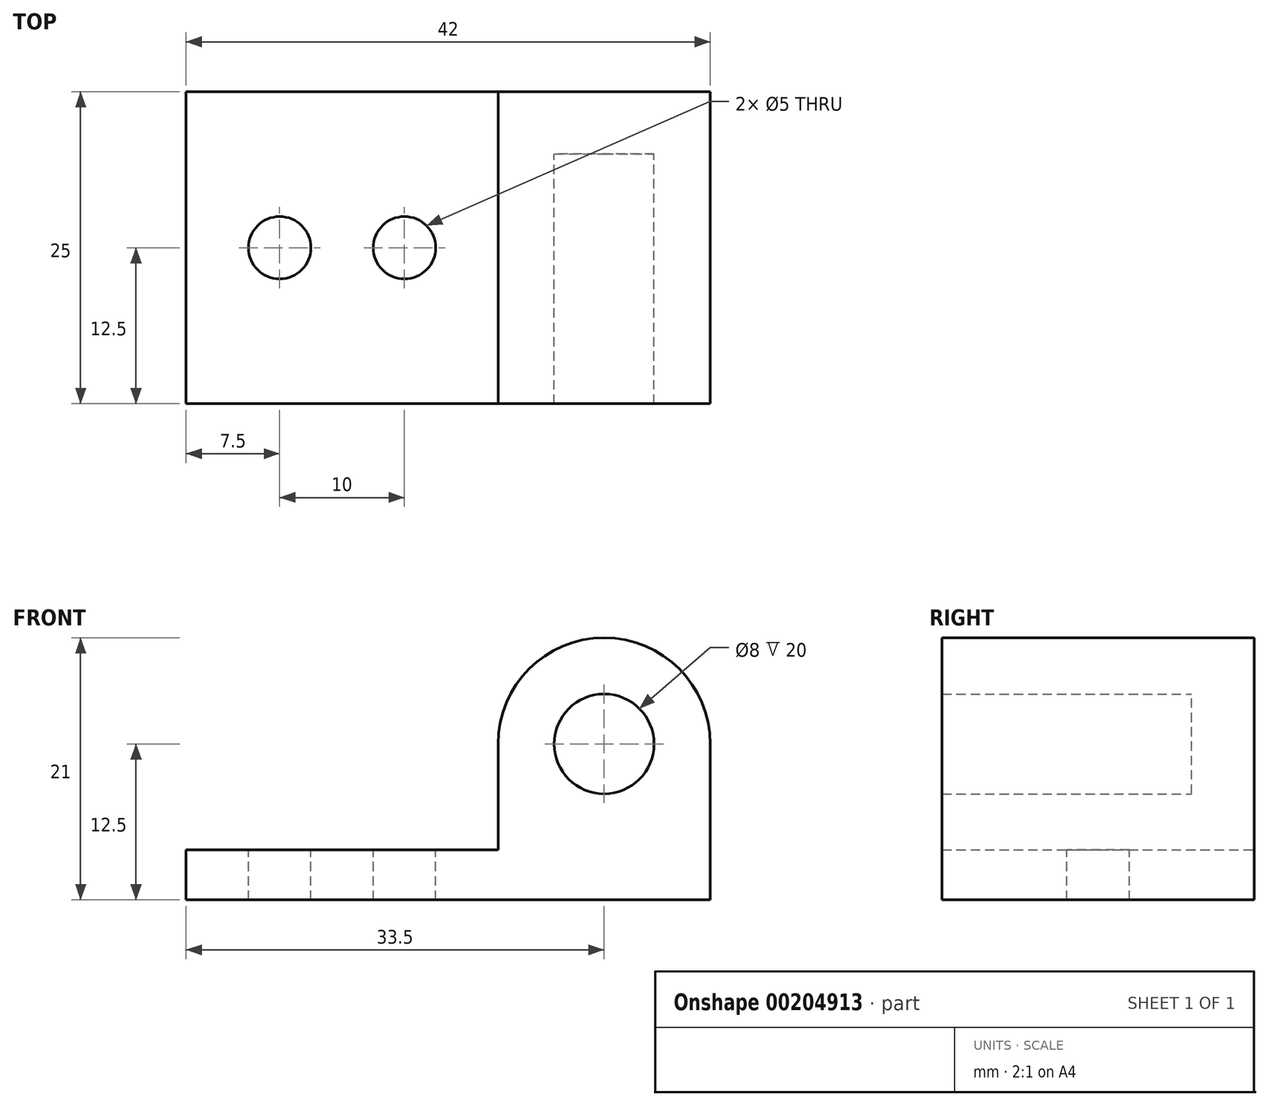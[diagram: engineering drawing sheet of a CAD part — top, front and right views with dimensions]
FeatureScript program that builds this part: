
annotation { "Feature Type Name" : "Feature", "Feature Type Description" : "" }
export const myFeature = defineFeature(function(context is Context, id is Id, definition is map)
    precondition{}
    {
        {
            var Q0;
            Q0=qCreatedBy(makeId("Front.planeOp"),FACE);
            var sketch = newSketch(context, id + "F0", { "sketchPlane" : qUnion([Q0])});
            skLineSegment(sketch, "E0", {"start": v(0, 0) * mm, "end": v(42, 0) * mm});
            skLineSegment(sketch, "E1", {"start": v(42, 0) * mm, "end": v(42, 4) * mm});
            skLineSegment(sketch, "E2", {"start": v(42, 4) * mm, "end": v(0, 4) * mm});
            skLineSegment(sketch, "E3", {"start": v(0, 4) * mm, "end": v(0, 0) * mm});
            skCircle(sketch, "E4", {"center": v(33.5, 12.5) * mm, "radius": 4 * mm});
            skCircle(sketch, "E5", {"center": v(33.5, 12.5) * mm, "radius": 8.5 * mm});
            skLineSegment(sketch, "E6", {"start": v(42, 4) * mm, "end": v(42, 21.37) * mm});
            skLineSegment(sketch, "E7", {"start": v(33.5, 12.5) * mm, "end": v(25, 12.5) * mm});
            skLineSegment(sketch, "E8", {"start": v(25, 12.5) * mm, "end": v(25, 4) * mm});
            skSolve(sketch);
        }
        {
            var Q0;
            Q0=makeQuery(id+"F0.imprint","IMPRINT",FACE,{"disambiguationData":[TD([[makeQuery(id+"F0.imprint","IMPRINT",EDGE,{"derivedFrom":sQuery(id+"F0.wireOp",EDGE,"E0")}),1.0]])]});
            var Q1;
            {var subQ3=sQuery(id+"F0.wireOp",EDGE,"E8");Q1=makeQuery(id+"F0.imprint","IMPRINT",FACE,{"disambiguationData":[TD([[makeQuery(id+"F0.imprint","IMPRINT",EDGE,{"derivedFrom":subQ3}),1.0]])]});}
            var Q2;
            Q2=makeQuery(id+"F0.imprint","IMPRINT",FACE,{"disambiguationData":[TD([[makeQuery(id+"F0.imprint","IMPRINT",EDGE,{"derivedFrom":sQuery(id+"F0.wireOp",EDGE,"E4")}),-1.0]])]});
            var Q3;
            {var subQ0=sQuery(id+"F0.wireOp",EDGE,"E6");var subQ3=sQuery(id+"F0.wireOp",EDGE,"E5");var subQ5=makeQuery(id+"F0.imprint","INTERSECT",VERTEX,{"derivedFrom":[subQ3,subQ0]});Q3=makeQuery(id+"F0.imprint","IMPRINT",FACE,{"disambiguationData":[TD([[makeQuery(id+"F0.imprint","IMPRINT",EDGE,{"disambiguationData":[TD([[subQ5,1.0]])],"derivedFrom":subQ3}),-1.0]])]});}
            extrude(context, id + "F1", {"entities" : qUnion([Q0, Q1, Q2, Q3]), "depth" : 25 * mm});
        }
        {
            var Q0;
            Q0=makeQuery(id+"F0.imprint","IMPRINT",FACE,{"disambiguationData":[TD([[makeQuery(id+"F0.imprint","IMPRINT",EDGE,{"derivedFrom":sQuery(id+"F0.wireOp",EDGE,"E4")}),1.0]])]});
            extrude(context, id + "F2", {"entities" : qUnion([Q0]), "operationType" : NewBodyOperationType.ADD, "depth" : 5 * mm});
        }
        {
            var Q0;
            Q0=makeQuery(id+"F1.opExtrude","SWEPT_FACE",FACE,{"disambiguationData":[OSD([sQuery(id+"F0.wireOp",EDGE,"E2")])]});
            var sketch = newSketch(context, id + "F3", { "sketchPlane" : qUnion([Q0])});
            skLineSegment(sketch, "E9", {"start": v(0, -12.5) * mm, "end": v(25, -12.5) * mm});
            skCircle(sketch, "E10", {"center": v(7.5, -12.5) * mm, "radius": 2.5 * mm});
            skCircle(sketch, "E11", {"center": v(17.5, -12.5) * mm, "radius": 2.5 * mm});
            skSolve(sketch);
        }
        {
            var Q0;
            {var subQ0=sQuery(id+"F3.wireOp",EDGE,"E10");var subQ1=sQuery(id+"F3.wireOp",EDGE,"E9");var subQ2=makeQuery(id+"F3.imprint","INTERSECT",VERTEX,{"disambiguationData":[OD(0.0)],"derivedFrom":[subQ1,subQ0]});Q0=makeQuery(id+"F3.imprint","IMPRINT",FACE,{"disambiguationData":[TD([[makeQuery(id+"F3.imprint","IMPRINT",EDGE,{"disambiguationData":[TD([[subQ2,-1.0]])],"derivedFrom":subQ1}),-1.0]])]});}
            var Q1;
            {var subQ0=sQuery(id+"F3.wireOp",EDGE,"E10");var subQ1=sQuery(id+"F3.wireOp",EDGE,"E9");var subQ2=makeQuery(id+"F3.imprint","INTERSECT",VERTEX,{"disambiguationData":[OD(0.0)],"derivedFrom":[subQ1,subQ0]});Q1=makeQuery(id+"F3.imprint","IMPRINT",FACE,{"disambiguationData":[TD([[makeQuery(id+"F3.imprint","IMPRINT",EDGE,{"disambiguationData":[TD([[subQ2,-1.0]])],"derivedFrom":subQ1}),1.0]])]});}
            var Q2;
            {var subQ0=sQuery(id+"F3.wireOp",EDGE,"E11");var subQ1=sQuery(id+"F3.wireOp",EDGE,"E9");var subQ2=makeQuery(id+"F3.imprint","INTERSECT",VERTEX,{"disambiguationData":[OD(0.0)],"derivedFrom":[subQ1,subQ0]});Q2=makeQuery(id+"F3.imprint","IMPRINT",FACE,{"disambiguationData":[TD([[makeQuery(id+"F3.imprint","IMPRINT",EDGE,{"disambiguationData":[TD([[subQ2,-1.0]])],"derivedFrom":subQ1}),-1.0]])]});}
            var Q3;
            {var subQ0=sQuery(id+"F3.wireOp",EDGE,"E11");var subQ1=sQuery(id+"F3.wireOp",EDGE,"E9");var subQ2=makeQuery(id+"F3.imprint","INTERSECT",VERTEX,{"disambiguationData":[OD(0.0)],"derivedFrom":[subQ1,subQ0]});Q3=makeQuery(id+"F3.imprint","IMPRINT",FACE,{"disambiguationData":[TD([[makeQuery(id+"F3.imprint","IMPRINT",EDGE,{"disambiguationData":[TD([[subQ2,-1.0]])],"derivedFrom":subQ1}),1.0]])]});}
            extrude(context, id + "F4", {"entities" : qUnion([Q0, Q1, Q2, Q3]), "operationType" : NewBodyOperationType.REMOVE, "oppositeDirection" : true, "depth" : 25 * mm});
        }
    });
